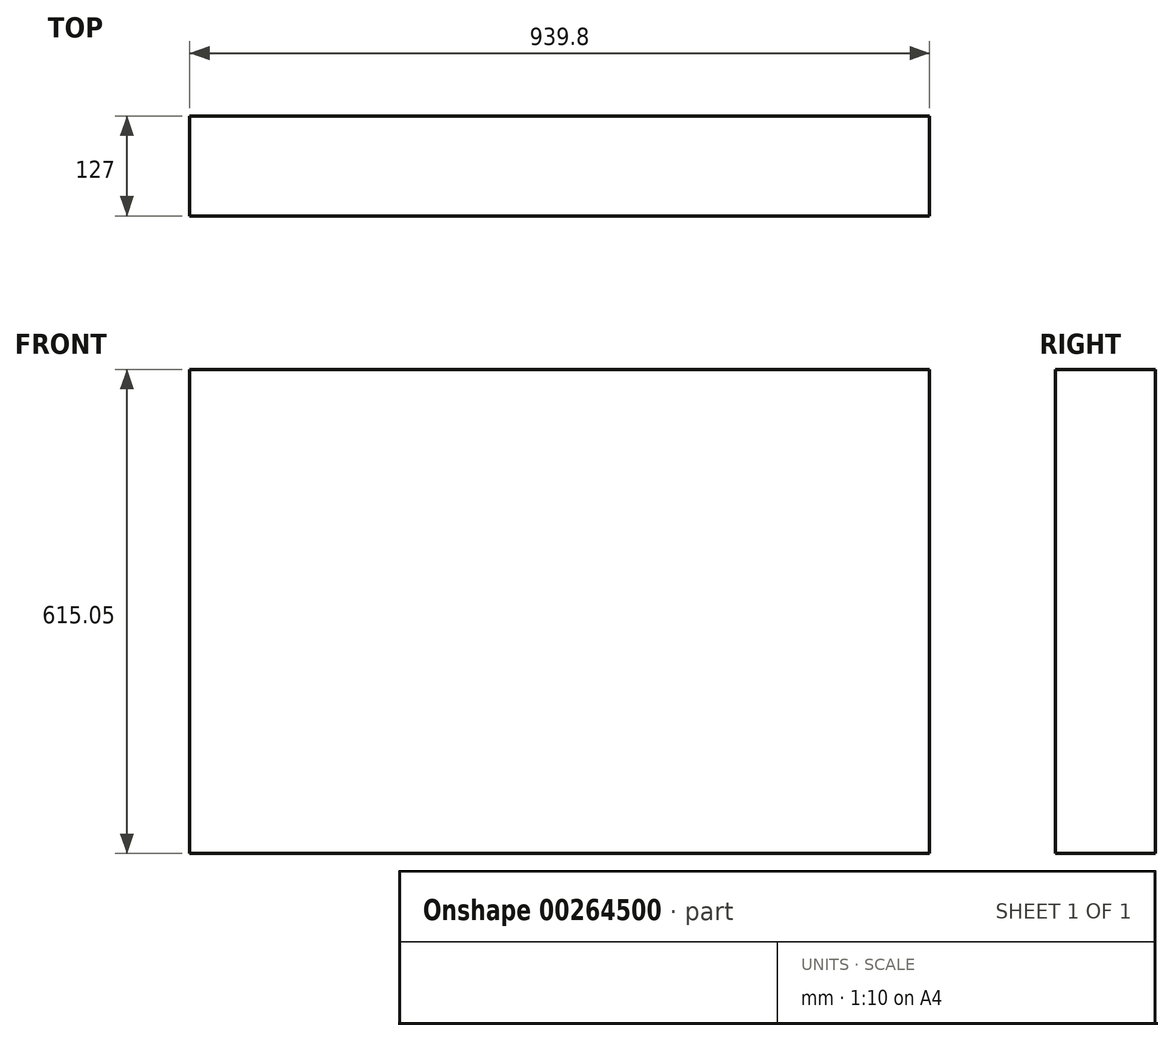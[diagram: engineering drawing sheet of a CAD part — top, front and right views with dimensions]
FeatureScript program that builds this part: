
annotation { "Feature Type Name" : "Feature", "Feature Type Description" : "" }
export const myFeature = defineFeature(function(context is Context, id is Id, definition is map)
    precondition{}
    {
        {
            var Q0;
            Q0=qCreatedBy(makeId("Top.planeOp"),FACE);
            var sketch = newSketch(context, id + "F0", { "sketchPlane" : qUnion([Q0])});
            skLineSegment(sketch, "E0.bottom", {"start": v(-469.9, 63.5) * mm, "end": v(469.9, 63.5) * mm});
            skLineSegment(sketch, "E0.top", {"start": v(-469.9, -63.5) * mm, "end": v(469.9, -63.5) * mm});
            skLineSegment(sketch, "E0.left", {"start": v(-469.9, 63.5) * mm, "end": v(-469.9, -63.5) * mm});
            skLineSegment(sketch, "E0.right", {"start": v(469.9, 63.5) * mm, "end": v(469.9, -63.5) * mm});
            skLineSegment(sketch, "E1", {"start": v(469.9, 0) * mm, "end": v(0, 0) * mm, "construction": true});
            skLineSegment(sketch, "E2", {"start": v(0, 0) * mm, "end": v(0, -63.5) * mm, "construction": true});
            skSolve(sketch);
        }
        {
            var Q0;
            Q0 = qSketchRegion(id + "F0", true);
            extrude(context, id + "F1", {"entities" : qUnion([Q0]), "depth" : 615.05 * mm});
        }
    });
